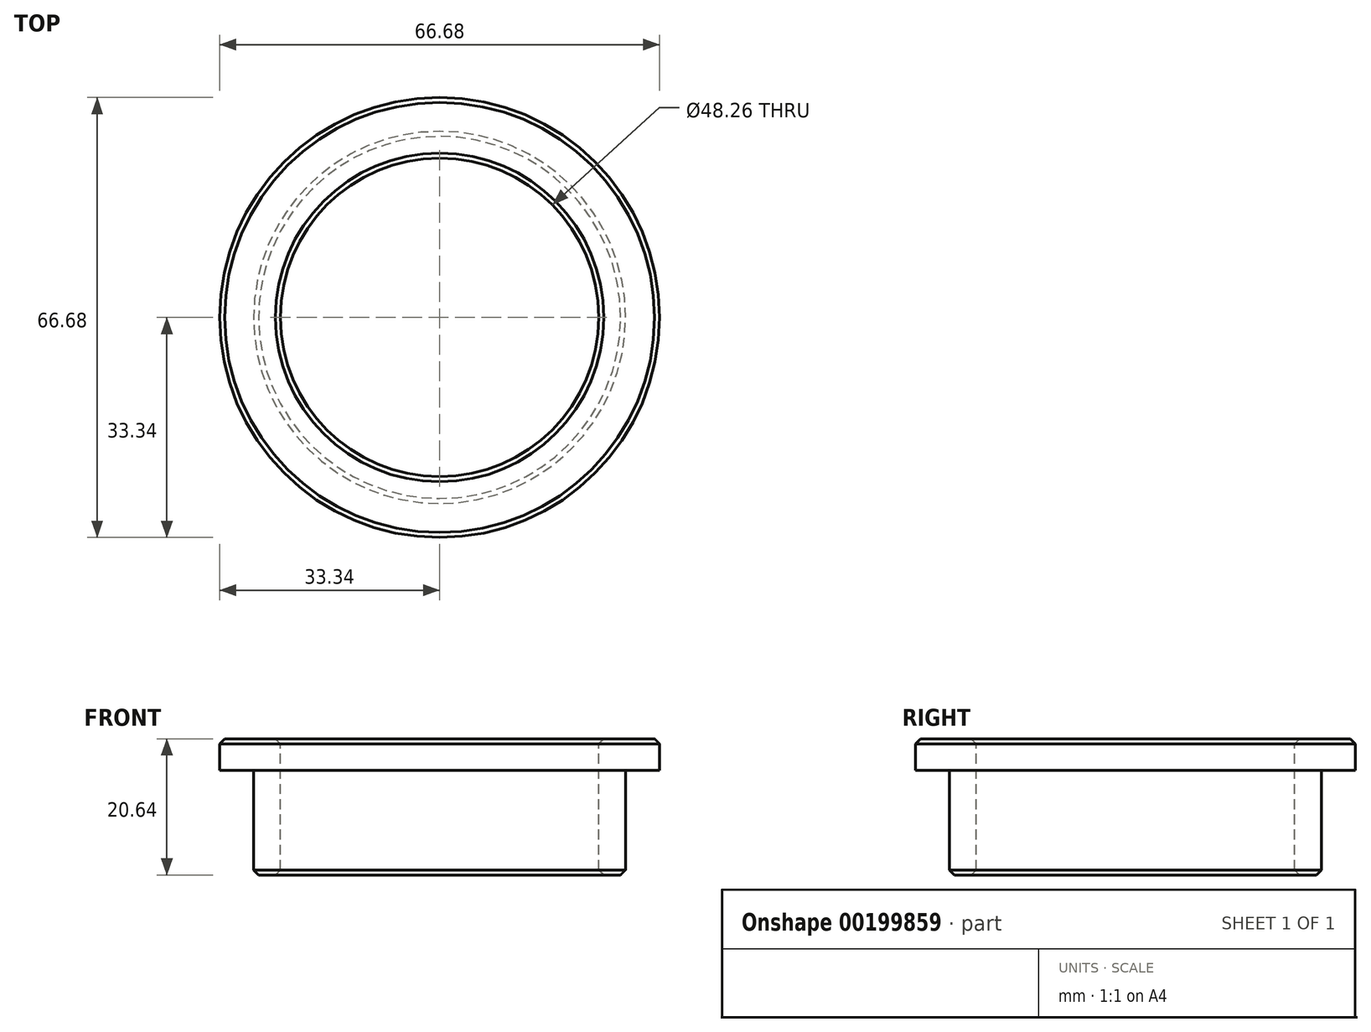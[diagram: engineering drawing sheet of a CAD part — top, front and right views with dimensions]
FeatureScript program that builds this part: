
annotation { "Feature Type Name" : "Feature", "Feature Type Description" : "" }
export const myFeature = defineFeature(function(context is Context, id is Id, definition is map)
    precondition{}
    {
        {
            var Q0;
            Q0=qCreatedBy(makeId("Top.planeOp"),FACE);
            var sketch = newSketch(context, id + "F0", { "sketchPlane" : qUnion([Q0])});
            skCircle(sketch, "E0", {"center": v(0, 0) * mm, "radius": 24.13 * mm});
            skCircle(sketch, "E1", {"center": v(0, 0) * mm, "radius": 28.2 * mm});
            skSolve(sketch);
        }
        {
            var Q0;
            Q0=makeQuery(id+"F0.imprint","IMPRINT",FACE,{"disambiguationData":[TD([[makeQuery(id+"F0.imprint","IMPRINT",EDGE,{"derivedFrom":sQuery(id+"F0.wireOp",EDGE,"E0")}),-1.0]])]});
            extrude(context, id + "F1", {"entities" : qUnion([Q0]), "oppositeDirection" : true, "depth" : 15.88 * mm});
        }
        {
            var Q0;
            Q0=qCreatedBy(makeId("Top.planeOp"),FACE);
            var sketch = newSketch(context, id + "F2", { "sketchPlane" : qUnion([Q0])});
            skCircle(sketch, "E2", {"center": v(0, 0) * mm, "radius": 33.34 * mm});
            skCircle(sketch, "E3.0", {"center": v(0, 0) * mm, "radius": 24.13 * mm});
            skSolve(sketch);
        }
        {
            var Q0;
            Q0=makeQuery(id+"F2.imprint","IMPRINT",FACE,{"disambiguationData":[TD([[makeQuery(id+"F2.imprint","IMPRINT",EDGE,{"derivedFrom":sQuery(id+"F2.wireOp",EDGE,"E2")}),1.0]])]});
            extrude(context, id + "F3", {"entities" : qUnion([Q0]), "operationType" : NewBodyOperationType.ADD, "depth" : 4.76 * mm});
        }
        {
            var Q0;
            Q0=makeQuery(id+"F3.opExtrude","CAP_EDGE",EDGE,{"disambiguationData":[OSD([sQuery(id+"F2.wireOp",EDGE,"E2")])],"isStart":false});
            var Q1;
            Q1=makeQuery(id+"F3.opExtrude","CAP_EDGE",EDGE,{"disambiguationData":[OSD([sQuery(id+"F2.wireOp",EDGE,"E3.0")])],"isStart":false});
            var Q2;
            Q2=makeQuery(id+"F1.opExtrude","CAP_EDGE",EDGE,{"disambiguationData":[OSD([sQuery(id+"F0.wireOp",EDGE,"E1")])],"isStart":false});
            var Q3;
            Q3=makeQuery(id+"F1.opExtrude","CAP_EDGE",EDGE,{"disambiguationData":[OSD([sQuery(id+"F0.wireOp",EDGE,"E0")])],"isStart":false});
            chamfer(context, id + "F4", {"entities" : qUnion([Q0, Q1, Q2, Q3]), "width" : 0.76 * mm, "tangentPropagation" : true});
        }
    });
